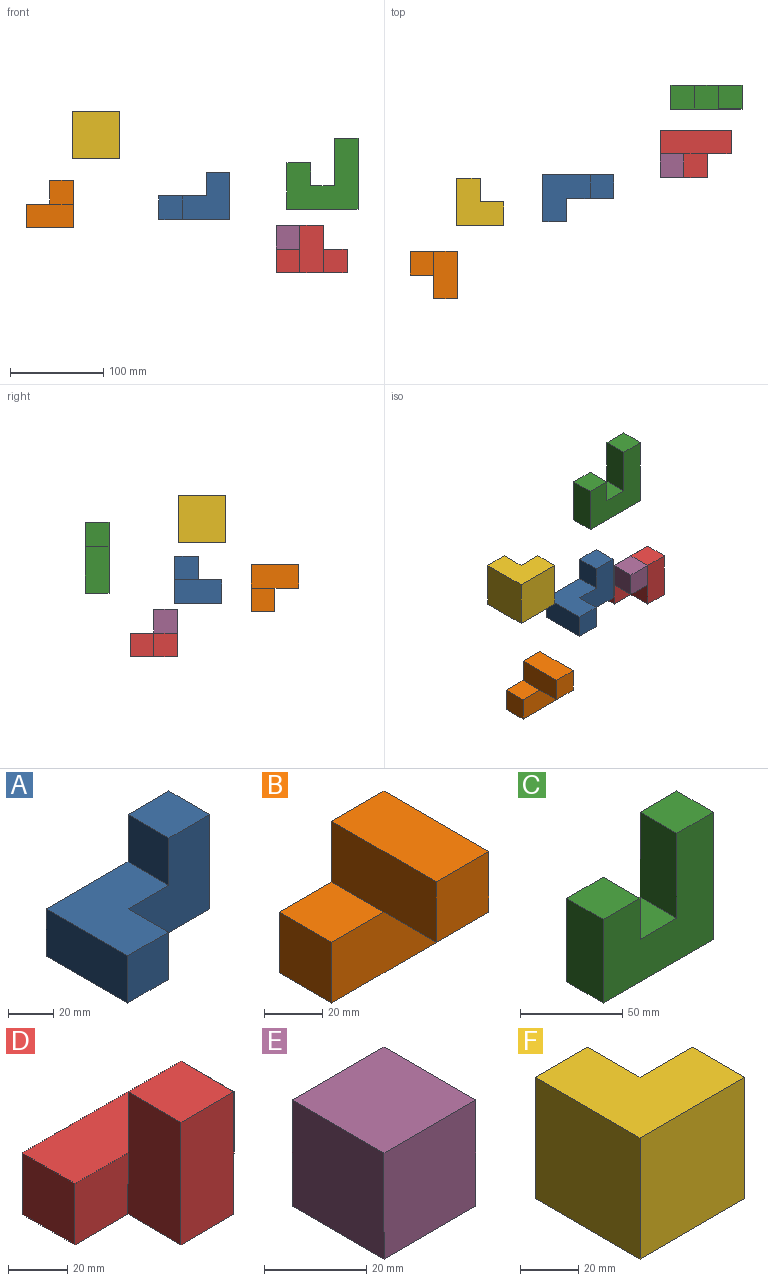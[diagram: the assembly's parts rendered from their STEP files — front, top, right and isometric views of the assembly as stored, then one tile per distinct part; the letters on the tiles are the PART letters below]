
ASSEMBLY  parts=6 mates=1
PART A: 10 faces, bbox 76.2x50.5x50.8 mm
  f0: plane 50.8x50.52mm, normal (0,0,1), area 1928.3mm2, adj f1,f2,f5,f6,f7,f8
  f1: plane 50.8x50.8mm, normal (0,-1,0), area 1935.5mm2, adj f0,f3,f4,f7,f8,f9
  f2: plane 50.52x25.4mm, normal (-1,0,0), area 1283.1mm2, adj f0,f3,f5,f6
  f3: plane 76.2x50.52mm, normal (0,0,-1), area 2573.4mm2, adj f1,f2,f4,f5,f6,f7
  f4: plane 50.8x25.4mm, normal (1,0,0), area 1290.3mm2, adj f1,f3,f5,f9
  f5: plane 76.2x50.8mm, normal (0,1,0), area 2580.6mm2, adj f0,f2,f3,f4,f8,f9
  f6: plane 25.4x25.4mm, normal (0,-1,0), area 645.2mm2, adj f0,f2,f3,f7
  f7: plane 25.4x25.12mm, normal (1,0,0), area 638mm2, adj f0,f1,f3,f6
  f8: plane 25.4x25.4mm, normal (-1,0,0), area 645.2mm2, adj f0,f1,f5,f9
  f9: plane 25.4x25.4mm, normal (0,0,1), area 645.2mm2, adj f1,f4,f5,f8
PART B: 10 faces, bbox 50.8x50.8x50.8 mm
  f0: plane 25.4x25.4mm, normal (0,0,1), area 645.2mm2, adj f1,f4,f5,f6
  f1: plane 25.4x25.4mm, normal (-1,0,0), area 645.2mm2, adj f0,f2,f4,f5
  f2: plane 50.8x25.4mm, normal (0,0,-1), area 1290.3mm2, adj f1,f3,f4,f5
  f3: plane 50.8x50.8mm, normal (1,0,0), area 1935.5mm2, adj f2,f4,f5,f7,f8,f9
  f4: plane 50.8x25.4mm, normal (0,-1,0), area 1290.3mm2, adj f0,f1,f2,f3,f8
  f5: plane 50.8x50.8mm, normal (0,1,0), area 1935.5mm2, adj f0,f1,f2,f3,f6,f7
  f6: plane 50.8x25.4mm, normal (-1,0,0), area 1290.3mm2, adj f0,f5,f7,f8,f9
  f7: plane 50.8x25.4mm, normal (0,0,1), area 1290.3mm2, adj f3,f5,f6,f9
  f8: plane 25.4x25.4mm, normal (0,0,-1), area 645.2mm2, adj f3,f4,f6,f9
  f9: plane 25.4x25.4mm, normal (0,-1,0), area 645.2mm2, adj f3,f6,f7,f8
PART C: 10 faces, bbox 76.2x25.4x76.2 mm
  f0: plane 25.4x25.4mm, normal (0,0,1), area 645.2mm2, adj f4,f5,f6,f8
  f1: plane 49.97x25.4mm, normal (-1,0,0), area 1269.3mm2, adj f2,f4,f5,f7
  f2: plane 76.2x25.4mm, normal (0,0,-1), area 1935.5mm2, adj f1,f3,f4,f5
  f3: plane 76.2x25.4mm, normal (1,0,0), area 1935.5mm2, adj f2,f4,f5,f9
  f4: plane 76.2x76.2mm, normal (0,-1,0), area 3849.9mm2, adj f0,f1,f2,f3,f6,f7,f8,f9
  f5: plane 76.2x76.2mm, normal (0,1,0), area 3849.9mm2, adj f0,f1,f2,f3,f6,f7,f8,f9
  f6: plane 25.4x24.57mm, normal (1,0,0), area 624.1mm2, adj f0,f4,f5,f7
  f7: plane 25.4x25.4mm, normal (0,0,1), area 645.2mm2, adj f1,f4,f5,f6
  f8: plane 50.8x25.4mm, normal (-1,0,0), area 1290.3mm2, adj f0,f4,f5,f9
  f9: plane 25.4x25.4mm, normal (0,0,1), area 645.2mm2, adj f3,f4,f5,f8
PART D: 12 faces, bbox 76.2x50.8x50.8 mm
  f0: plane 76.2x25.4mm, normal (0,0,1), area 1935.5mm2, adj f1,f2,f4,f5,f6,f10
  f1: plane 25.4x25.4mm, normal (0,-1,0), area 645.2mm2, adj f0,f3,f6,f7
  f2: plane 25.4x25.4mm, normal (0,-1,0), area 645.2mm2, adj f0,f3,f5,f8
  f3: plane 76.2x50.8mm, normal (0,0,-1), area 2580.6mm2, adj f1,f2,f4,f5,f6,f7,f8,f9
  f4: plane 76.2x25.4mm, normal (0,1,0), area 1935.5mm2, adj f0,f3,f5,f6
  f5: plane 25.4x25.4mm, normal (1,0,0), area 645.2mm2, adj f0,f2,f3,f4
  f6: plane 25.4x25.4mm, normal (-1,0,0), area 645.2mm2, adj f0,f1,f3,f4
  f7: plane 50.8x25.4mm, normal (-1,0,0), area 1290.3mm2, adj f1,f3,f9,f10,f11
  f8: plane 50.8x25.4mm, normal (1,0,0), area 1290.3mm2, adj f2,f3,f9,f10,f11
  f9: plane 50.8x25.4mm, normal (0,-1,0), area 1290.3mm2, adj f3,f7,f8,f11
  f10: plane 25.4x25.4mm, normal (0,1,0), area 645.2mm2, adj f0,f7,f8,f11
  f11: plane 25.4x25.4mm, normal (0,0,1), area 645.2mm2, adj f7,f8,f9,f10
PART E: 6 faces, bbox 25.4x25.4x25.4 mm
  f0: plane 25.4x25.4mm, normal (-1,0,0), area 645.2mm2, adj f1,f3,f4,f5
  f1: plane 25.4x25.4mm, normal (0,0,-1), area 645.2mm2, adj f0,f2,f4,f5
  f2: plane 25.4x25.4mm, normal (1,0,0), area 645.2mm2, adj f1,f3,f4,f5
  f3: plane 25.4x25.4mm, normal (0,0,1), area 645.2mm2, adj f0,f2,f4,f5
  f4: plane 25.4x25.4mm, normal (0,-1,0), area 645.2mm2, adj f0,f1,f2,f3
  f5: plane 25.4x25.4mm, normal (0,1,0), area 645.2mm2, adj f0,f1,f2,f3
PART F: 8 faces, bbox 50.8x50.8x50.8 mm
  f0: plane 50.8x50.8mm, normal (0,-1,0), area 2580.6mm2, adj f3,f4,f5,f6
  f1: plane 50.8x25.4mm, normal (1,0,0), area 1290.3mm2, adj f2,f4,f5,f7
  f2: plane 50.8x25.4mm, normal (0,1,0), area 1290.3mm2, adj f1,f3,f4,f5
  f3: plane 50.8x50.8mm, normal (-1,0,0), area 2580.6mm2, adj f0,f2,f4,f5
  f4: plane 50.8x50.8mm, normal (0,0,1), area 1935.5mm2, adj f0,f1,f2,f3,f6,f7
  f5: plane 50.8x50.8mm, normal (0,0,-1), area 1935.5mm2, adj f0,f1,f2,f3,f6,f7
  f6: plane 50.8x25.4mm, normal (1,0,0), area 1290.3mm2, adj f0,f4,f5,f7
  f7: plane 50.8x25.4mm, normal (0,1,0), area 1290.3mm2, adj f1,f4,f5,f6
PLACE A t=(-64.27,24.17,15.5)mm
PLACE B t=(-207.69,-57.97,6.97)mm
PLACE C t=(73.26,120.12,26.6)mm
PLACE D t=(61.61,46.78,-41.57)mm
PLACE E t=(61.61,46.78,-16.17)mm
PLACE F t=(-131.44,-30.41,80.92)mm
MATE revolute E.f1 <-> D.f0  axis (0,0,1) through (87.01,46.78,-16.17)mm
